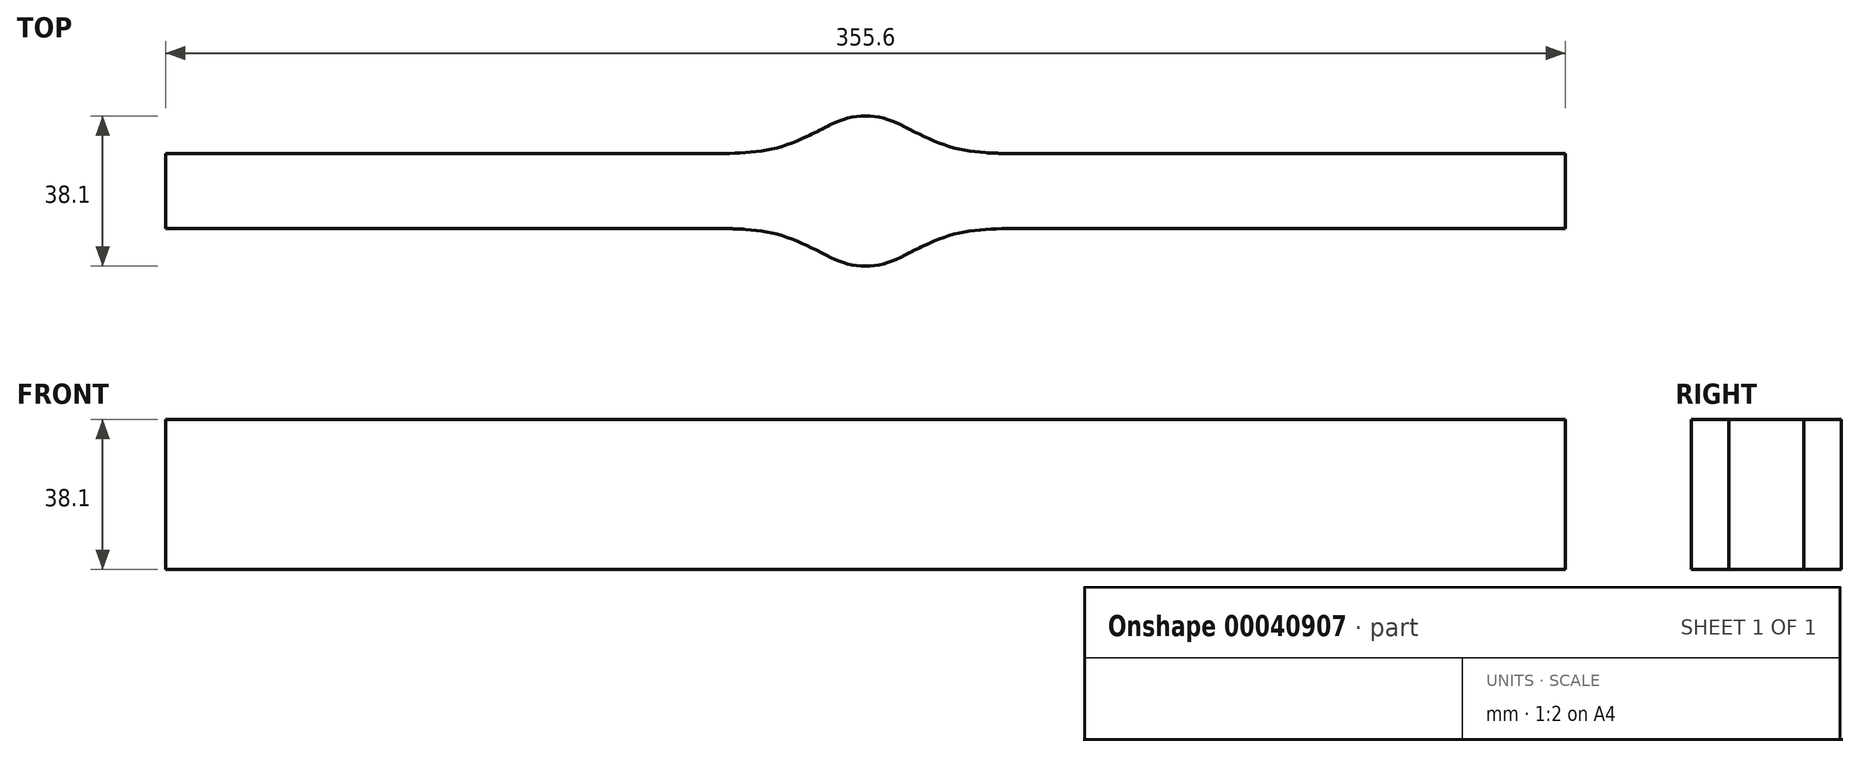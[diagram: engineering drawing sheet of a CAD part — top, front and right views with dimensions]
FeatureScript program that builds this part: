
annotation { "Feature Type Name" : "Feature", "Feature Type Description" : "" }
export const myFeature = defineFeature(function(context is Context, id is Id, definition is map)
    precondition{}
    {
        {
            var Q0;
            Q0=qCreatedBy(makeId("Top.planeOp"),FACE);
            var sketch = newSketch(context, id + "F0", { "sketchPlane" : qUnion([Q0])});
            skLineSegment(sketch, "E0.bottom", {"start": v(177.8, -9.52) * mm, "end": v(16.5, -9.53) * mm});
            skLineSegment(sketch, "E0.top", {"start": v(177.8, 9.53) * mm, "end": v(16.5, 9.53) * mm});
            skLineSegment(sketch, "E0.left", {"start": v(177.8, -9.52) * mm, "end": v(177.8, 9.53) * mm});
            skLineSegment(sketch, "E0.right", {"start": v(-177.8, -9.53) * mm, "end": v(-177.8, 9.52) * mm});
            skPoint(sketch, "E0.middle", {"position": v(0, 0) * mm});
            skCircle(sketch, "E1", {"center": v(0, 0) * mm, "radius": 7.94 * mm});
            skArc(sketch, "E2", {"start": v(16.5, 9.53) * mm, "mid": v(0, 19.05) * mm, "end": v(-16.5, 9.53) * mm});
            skLineSegment(sketch, "E3", {"start": v(-16.5, 9.53) * mm, "end": v(-16.5, 9.53) * mm});
            skLineSegment(sketch, "E4", {"start": v(-16.5, -9.53) * mm, "end": v(-177.8, -9.53) * mm});
            skArc(sketch, "E5", {"start": v(-16.5, -9.53) * mm, "mid": v(0, -19.05) * mm, "end": v(16.5, -9.53) * mm});
            skLineSegment(sketch, "E6", {"start": v(-16.5, 9.53) * mm, "end": v(-177.8, 9.52) * mm});
            skSolve(sketch);
        }
        {
            var Q0;
            Q0=makeQuery(id+"F0.imprint","IMPRINT",FACE,{"disambiguationData":[TD([[makeQuery(id+"F0.imprint","IMPRINT",EDGE,{"derivedFrom":sQuery(id+"F0.wireOp",EDGE,"E0.bottom")}),-1.0]])]});
            var Q1;
            Q1=makeQuery(id+"F0.imprint","IMPRINT",FACE,{"disambiguationData":[TD([[makeQuery(id+"F0.imprint","IMPRINT",EDGE,{"derivedFrom":sQuery(id+"F0.wireOp",EDGE,"E1")}),1.0]])]});
            extrude(context, id + "F1", {"entities" : qUnion([Q0, Q1]), "depth" : 38.1 * mm, "offsetDistance" : 25.4 * mm});
        }
        {
            var Q0;
            Q0=makeQuery(id+"F1.opExtrude","SWEPT_EDGE",EDGE,{"disambiguationData":[OSD([sQuery(id+"F0.wireOp",EDGE,"E0.right"),sQuery(id+"F0.wireOp",EDGE,"E4")])]});
            var Q1;
            Q1=makeQuery(id+"F1.opExtrude","SWEPT_EDGE",EDGE,{"disambiguationData":[OSD([sQuery(id+"F0.wireOp",EDGE,"E0.right"),sQuery(id+"F0.wireOp",EDGE,"E6")])]});
            var Q2;
            Q2=makeQuery(id+"F1.opExtrude","SWEPT_EDGE",EDGE,{"disambiguationData":[OSD([sQuery(id+"F0.wireOp",EDGE,"E0.top"),sQuery(id+"F0.wireOp",EDGE,"E0.left")])]});
            var Q3;
            Q3=makeQuery(id+"F1.opExtrude","SWEPT_EDGE",EDGE,{"disambiguationData":[OSD([sQuery(id+"F0.wireOp",EDGE,"E0.bottom"),sQuery(id+"F0.wireOp",EDGE,"E0.left")])]});
            fillet(context, id + "F2", {"entities" : qUnion([Q0, Q1, Q2, Q3]), "radius" : 3 / 203.2 * mm, "tangentPropagation" : true, "rho" : .65, "crossSection" : FilletCrossSection.CONIC, "allowEdgeOverflow" : false});
        }
        {
            var Q0;
            Q0=makeQuery(id+"F1.opExtrude","SWEPT_EDGE",EDGE,{"disambiguationData":[OSD([sQuery(id+"F0.wireOp",EDGE,"E0.top"),sQuery(id+"F0.wireOp",EDGE,"E2")])]});
            var Q1;
            Q1=makeQuery(id+"F1.opExtrude","SWEPT_EDGE",EDGE,{"disambiguationData":[OSD([sQuery(id+"F0.wireOp",EDGE,"E2"),sQuery(id+"F0.wireOp",EDGE,"E6")])]});
            var Q2;
            Q2=makeQuery(id+"F1.opExtrude","SWEPT_EDGE",EDGE,{"disambiguationData":[OSD([sQuery(id+"F0.wireOp",EDGE,"E4"),sQuery(id+"F0.wireOp",EDGE,"E5")])]});
            var Q3;
            Q3=makeQuery(id+"F1.opExtrude","SWEPT_EDGE",EDGE,{"disambiguationData":[OSD([sQuery(id+"F0.wireOp",EDGE,"E0.bottom"),sQuery(id+"F0.wireOp",EDGE,"E5")])]});
            fillet(context, id + "F3", {"entities" : qUnion([Q0, Q1, Q2, Q3]), "radius" : 64.03 * mm, "tangentPropagation" : true, "rho" : 0.65, "crossSection" : FilletCrossSection.CONIC, "allowEdgeOverflow" : false});
        }
    });
